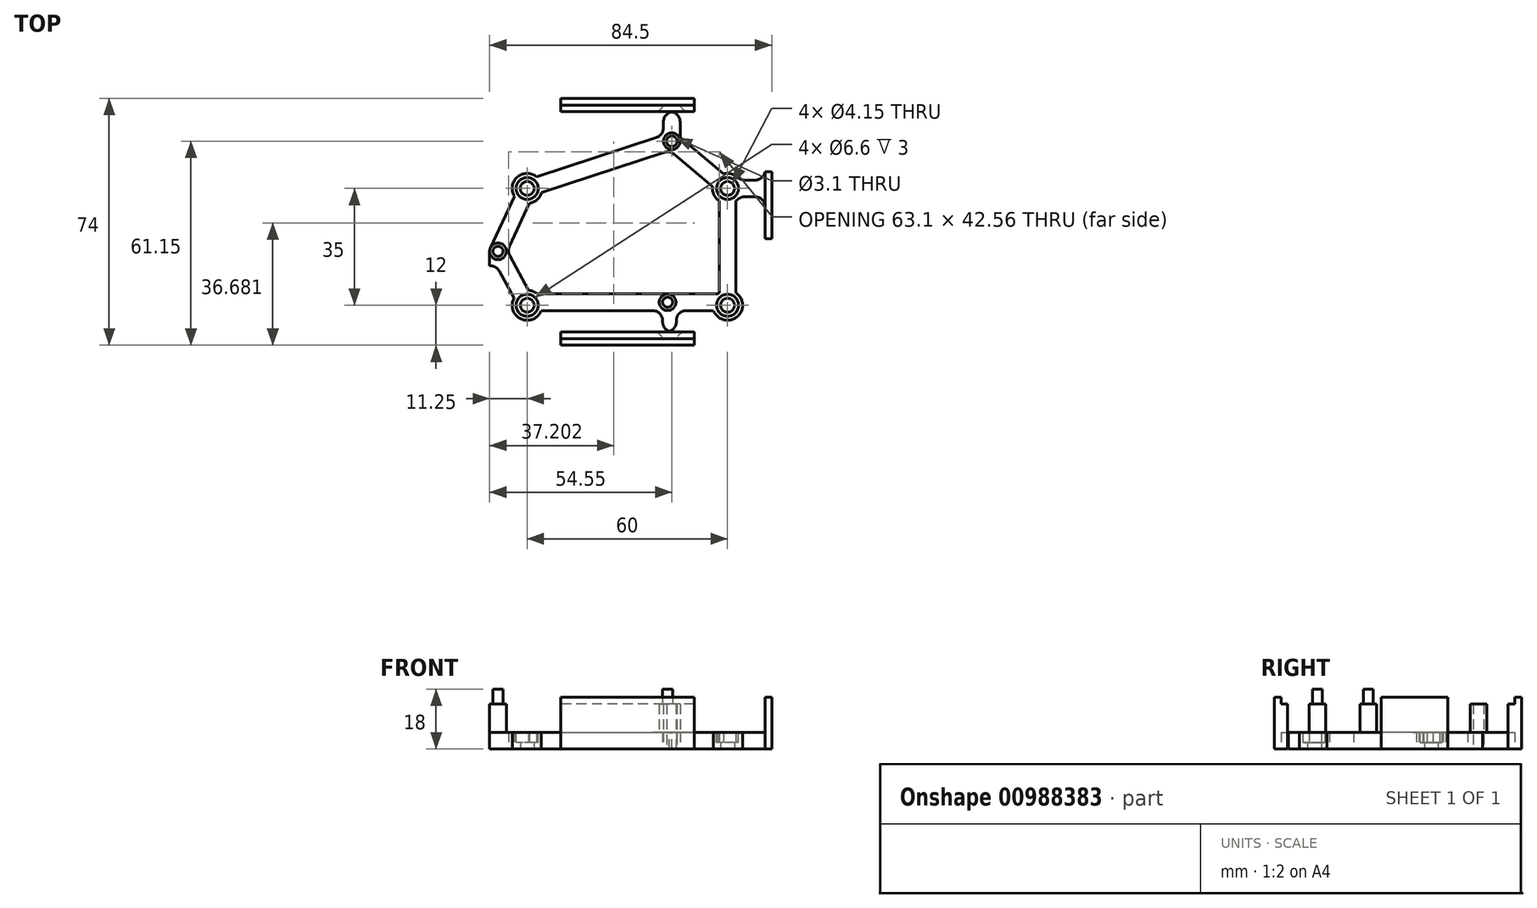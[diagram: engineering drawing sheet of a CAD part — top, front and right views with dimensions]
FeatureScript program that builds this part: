
annotation { "Feature Type Name" : "Feature", "Feature Type Description" : "" }
export const myFeature = defineFeature(function(context is Context, id is Id, definition is map)
    precondition{}
    {
        {
            var Q0;
            Q0=qCreatedBy(makeId("Top.planeOp"),FACE);
            var sketch = newSketch(context, id + "F0", { "sketchPlane" : qUnion([Q0])});
            skLineSegment(sketch, "E0.bottom", {"start": v(-41.25, 35) * mm, "end": v(41.25, 35) * mm});
            skLineSegment(sketch, "E0.top", {"start": v(-41.25, -35) * mm, "end": v(41.25, -35) * mm});
            skLineSegment(sketch, "E0.left", {"start": v(-41.25, 35) * mm, "end": v(-41.25, -35) * mm});
            skLineSegment(sketch, "E0.right", {"start": v(41.25, 35) * mm, "end": v(41.25, -35) * mm});
            skPoint(sketch, "E1", {"position": v(0, 35) * mm});
            skPoint(sketch, "E2", {"position": v(-41.25, 0) * mm});
            skCircle(sketch, "E3", {"center": v(13.3, 24.15) * mm, "radius": 1.55 * mm});
            skCircle(sketch, "E4", {"center": v(12.05, -24.1) * mm, "radius": 1.5 * mm});
            skCircle(sketch, "E5", {"center": v(-38.75, -8.85) * mm, "radius": 1.5 * mm});
            skCircle(sketch, "E6", {"center": v(-30, 10) * mm, "radius": 2.08 * mm});
            skCircle(sketch, "E7", {"center": v(30, 10) * mm, "radius": 2.08 * mm});
            skCircle(sketch, "E8", {"center": v(-30, -25) * mm, "radius": 2.08 * mm});
            skCircle(sketch, "E9", {"center": v(30, -25) * mm, "radius": 2.08 * mm});
            skLineSegment(sketch, "E10.bottom", {"start": v(-30, 10) * mm, "end": v(30, 10) * mm, "construction": true});
            skLineSegment(sketch, "E10.top", {"start": v(-30, -25) * mm, "end": v(30, -25) * mm, "construction": true});
            skLineSegment(sketch, "E10.left", {"start": v(-30, 10) * mm, "end": v(-30, -25) * mm, "construction": true});
            skLineSegment(sketch, "E10.right", {"start": v(30, 10) * mm, "end": v(30, -25) * mm, "construction": true});
            skPoint(sketch, "E11", {"position": v(0, 10) * mm});
            skPoint(sketch, "E12", {"position": v(30, -7.5) * mm});
            skLineSegment(sketch, "E13", {"start": v(-38.75, -8.85) * mm, "end": v(0, 0) * mm, "construction": true});
            skLineSegment(sketch, "E14", {"start": v(0, 0) * mm, "end": v(12.05, -24.1) * mm, "construction": true});
            skLineSegment(sketch, "E15", {"start": v(0, 0) * mm, "end": v(13.3, 24.15) * mm, "construction": true});
            skLineSegment(sketch, "E16", {"start": v(-30, 10) * mm, "end": v(13.3, 24.15) * mm, "construction": true});
            skLineSegment(sketch, "E17", {"start": v(13.3, 24.15) * mm, "end": v(30, 10) * mm, "construction": true});
            skLineSegment(sketch, "E18", {"start": v(-30, -25) * mm, "end": v(-38.75, -8.85) * mm, "construction": true});
            skLineSegment(sketch, "E19", {"start": v(-38.75, -8.85) * mm, "end": v(-30, 10) * mm, "construction": true});
            skCircle(sketch, "E20", {"center": v(-30, 10) * mm, "radius": 4.5 * mm});
            skCircle(sketch, "E21", {"center": v(30, 10) * mm, "radius": 4.5 * mm});
            skCircle(sketch, "E22", {"center": v(30, -25) * mm, "radius": 4.5 * mm});
            skCircle(sketch, "E23", {"center": v(-30, -25) * mm, "radius": 4.5 * mm});
            skCircle(sketch, "E24", {"center": v(-38.75, -8.85) * mm, "radius": 2.5 * mm});
            skCircle(sketch, "E25", {"center": v(13.3, 24.15) * mm, "radius": 2.5 * mm});
            skCircle(sketch, "E26", {"center": v(12.05, -24.1) * mm, "radius": 2.5 * mm});
            skLineSegment(sketch, "E27", {"start": v(-27.22, 13.54) * mm, "end": v(12.52, 26.53) * mm});
            skLineSegment(sketch, "E28", {"start": v(-25.67, 8.79) * mm, "end": v(14.08, 21.77) * mm});
            skLineSegment(sketch, "E29", {"start": v(28.76, 14.33) * mm, "end": v(14.92, 26.06) * mm});
            skLineSegment(sketch, "E30", {"start": v(25.53, 10.51) * mm, "end": v(11.68, 22.24) * mm});
            skLineSegment(sketch, "E31", {"start": v(27.5, 6.26) * mm, "end": v(27.5, -21.26) * mm});
            skLineSegment(sketch, "E32", {"start": v(32.5, 6.26) * mm, "end": v(32.5, -21.26) * mm});
            skLineSegment(sketch, "E33", {"start": v(27.05, -21.6) * mm, "end": v(12.05, -21.6) * mm});
            skLineSegment(sketch, "E34", {"start": v(12.05, -24.1) * mm, "end": v(30, -25) * mm, "construction": true});
            skLineSegment(sketch, "E35", {"start": v(12.05, -24.1) * mm, "end": v(-30, -25) * mm, "construction": true});
            skLineSegment(sketch, "E36", {"start": v(-27.05, -21.6) * mm, "end": v(12.05, -21.6) * mm});
            skLineSegment(sketch, "E37", {"start": v(-25.8, -26.6) * mm, "end": v(12.05, -26.6) * mm});
            skLineSegment(sketch, "E38", {"start": v(-29.58, -20.52) * mm, "end": v(-36.55, -7.66) * mm});
            skLineSegment(sketch, "E39", {"start": v(-33.98, -22.9) * mm, "end": v(-40.95, -10.04) * mm});
            skLineSegment(sketch, "E40", {"start": v(-33.84, 7.66) * mm, "end": v(-41.02, -7.8) * mm});
            skLineSegment(sketch, "E41", {"start": v(-29.3, 5.55) * mm, "end": v(-36.48, -9.9) * mm});
            skPoint(sketch, "E42", {"position": v(12.75, 21.34) * mm});
            skLineSegment(sketch, "E43", {"start": v(12.05, -26.6) * mm, "end": v(25.8, -26.6) * mm});
            skPoint(sketch, "E44", {"position": v(11.99, -26.6) * mm});
            skLineSegment(sketch, "E45.bottom", {"start": v(-20, -35) * mm, "end": v(20, -35) * mm});
            skLineSegment(sketch, "E45.top", {"start": v(-20, -37) * mm, "end": v(20, -37) * mm});
            skLineSegment(sketch, "E45.left", {"start": v(-20, -35) * mm, "end": v(-20, -37) * mm});
            skLineSegment(sketch, "E45.right", {"start": v(20, -35) * mm, "end": v(20, -37) * mm});
            skPoint(sketch, "E46", {"position": v(0, -37) * mm});
            skLineSegment(sketch, "E47.bottom", {"start": v(-20, 35) * mm, "end": v(20, 35) * mm});
            skLineSegment(sketch, "E47.top", {"start": v(-20, 37) * mm, "end": v(20, 37) * mm});
            skLineSegment(sketch, "E47.left", {"start": v(-20, 35) * mm, "end": v(-20, 37) * mm});
            skLineSegment(sketch, "E47.right", {"start": v(20, 35) * mm, "end": v(20, 37) * mm});
            skPoint(sketch, "E48", {"position": v(0, 37) * mm});
            skLineSegment(sketch, "E49.bottom", {"start": v(41.25, 15) * mm, "end": v(43.25, 15) * mm});
            skLineSegment(sketch, "E49.top", {"start": v(41.25, -5) * mm, "end": v(43.25, -5) * mm});
            skLineSegment(sketch, "E49.left", {"start": v(41.25, 15) * mm, "end": v(41.25, -5) * mm});
            skLineSegment(sketch, "E49.right", {"start": v(43.25, 15) * mm, "end": v(43.25, -5) * mm});
            skLineSegment(sketch, "E50.bottom", {"start": v(-41.25, -35) * mm, "end": v(-39.25, -35) * mm});
            skLineSegment(sketch, "E50.top", {"start": v(-41.25, -13.18) * mm, "end": v(-39.25, -13.18) * mm});
            skLineSegment(sketch, "E50.left", {"start": v(-41.25, -35) * mm, "end": v(-41.25, -13.18) * mm});
            skLineSegment(sketch, "E50.right", {"start": v(-39.25, -35) * mm, "end": v(-39.25, -13.18) * mm});
            skLineSegment(sketch, "E51", {"start": v(10.55, -26.1) * mm, "end": v(10.55, -35) * mm});
            skLineSegment(sketch, "E52", {"start": v(14.55, -24.05) * mm, "end": v(14.78, -35) * mm});
            skLineSegment(sketch, "E53", {"start": v(33.74, 12.5) * mm, "end": v(41.25, 12.5) * mm});
            skLineSegment(sketch, "E54", {"start": v(33.74, 7.5) * mm, "end": v(41.25, 7.5) * mm});
            skLineSegment(sketch, "E55", {"start": v(41.25, 12.5) * mm, "end": v(41.25, 7.5) * mm, "construction": true});
            skPoint(sketch, "E56", {"position": v(41.25, 10) * mm});
            skLineSegment(sketch, "E57", {"start": v(10.8, 24.15) * mm, "end": v(10.8, 35) * mm});
            skLineSegment(sketch, "E58", {"start": v(15.8, 24.15) * mm, "end": v(15.8, 35) * mm});
            skLineSegment(sketch, "E59.top", {"start": v(-20, -33) * mm, "end": v(20, -33) * mm});
            skLineSegment(sketch, "E59.left", {"start": v(-20, -35) * mm, "end": v(-20, -33) * mm});
            skLineSegment(sketch, "E59.right", {"start": v(20, -35) * mm, "end": v(20, -33) * mm});
            skLineSegment(sketch, "E60.top", {"start": v(-20, 33) * mm, "end": v(20, 33) * mm});
            skLineSegment(sketch, "E60.left", {"start": v(-20, 35) * mm, "end": v(-20, 33) * mm});
            skLineSegment(sketch, "E60.right", {"start": v(20, 35) * mm, "end": v(20, 33) * mm});
            skSolve(sketch);
        }
        {
            var Q0;
            {var subQ1=sQuery(id+"F0.wireOp",EDGE,"E20");var subQ9=sQuery(id+"F0.wireOp",EDGE,"E27");var subQ10=makeQuery(id+"F0.imprint","INTERSECT",VERTEX,{"derivedFrom":[subQ1,subQ9]});Q0=makeQuery(id+"F0.imprint","IMPRINT",FACE,{"disambiguationData":[TD([[makeQuery(id+"F0.imprint","IMPRINT",EDGE,{"disambiguationData":[TD([[subQ10,1.0]])],"derivedFrom":subQ1}),-1.0]])]});}
            var Q1;
            Q1=makeQuery(id+"F0.imprint","IMPRINT",FACE,{"disambiguationData":[TD([[makeQuery(id+"F0.imprint","IMPRINT",EDGE,{"derivedFrom":sQuery(id+"F0.wireOp",EDGE,"E6")}),-1.0]])]});
            var Q2;
            {var subQ0=sQuery(id+"F0.wireOp",EDGE,"E40");Q2=makeQuery(id+"F0.imprint","IMPRINT",FACE,{"disambiguationData":[TD([[makeQuery(id+"F0.imprint","IMPRINT",EDGE,{"derivedFrom":subQ0}),1.0]])]});}
            var Q3;
            Q3=makeQuery(id+"F0.imprint","IMPRINT",FACE,{"disambiguationData":[TD([[makeQuery(id+"F0.imprint","IMPRINT",EDGE,{"derivedFrom":sQuery(id+"F0.wireOp",EDGE,"E5")}),-1.0]])]});
            var Q4;
            {var subQ0=sQuery(id+"F0.wireOp",EDGE,"E50.top");Q4=makeQuery(id+"F0.imprint","IMPRINT",FACE,{"disambiguationData":[TD([[makeQuery(id+"F0.imprint","IMPRINT",EDGE,{"derivedFrom":subQ0}),1.0]])]});}
            var Q5;
            {var subQ0=sQuery(id+"F0.wireOp",EDGE,"E38");var subQ1=sQuery(id+"F0.wireOp",EDGE,"E24");var subQ2=makeQuery(id+"F0.imprint","INTERSECT",VERTEX,{"derivedFrom":[subQ1,subQ0]});Q5=makeQuery(id+"F0.imprint","IMPRINT",FACE,{"disambiguationData":[TD([[makeQuery(id+"F0.imprint","IMPRINT",EDGE,{"disambiguationData":[TD([[subQ2,1.0]])],"derivedFrom":subQ1}),-1.0]])]});}
            var Q6;
            {var subQ1=sQuery(id+"F0.wireOp",EDGE,"E23");var subQ8=sQuery(id+"F0.wireOp",EDGE,"E38");var subQ9=makeQuery(id+"F0.imprint","INTERSECT",VERTEX,{"derivedFrom":[subQ1,subQ8]});Q6=makeQuery(id+"F0.imprint","IMPRINT",FACE,{"disambiguationData":[TD([[makeQuery(id+"F0.imprint","IMPRINT",EDGE,{"disambiguationData":[TD([[subQ9,-1.0]])],"derivedFrom":subQ1}),-1.0]])]});}
            var Q7;
            Q7=makeQuery(id+"F0.imprint","IMPRINT",FACE,{"disambiguationData":[TD([[makeQuery(id+"F0.imprint","IMPRINT",EDGE,{"derivedFrom":sQuery(id+"F0.wireOp",EDGE,"E50.bottom")}),1.0]])]});
            var Q8;
            Q8=makeQuery(id+"F0.imprint","IMPRINT",FACE,{"disambiguationData":[TD([[makeQuery(id+"F0.imprint","IMPRINT",EDGE,{"derivedFrom":sQuery(id+"F0.wireOp",EDGE,"E8")}),-1.0]])]});
            var Q9;
            {var subQ0=sQuery(id+"F0.wireOp",EDGE,"E36");Q9=makeQuery(id+"F0.imprint","IMPRINT",FACE,{"disambiguationData":[TD([[makeQuery(id+"F0.imprint","IMPRINT",EDGE,{"derivedFrom":subQ0}),-1.0]])]});}
            var Q10;
            {var subQ0=sQuery(id+"F0.wireOp",EDGE,"E43");var subQ1=sQuery(id+"F0.wireOp",EDGE,"E26");var subQ2=makeQuery(id+"F0.imprint","INTERSECT",VERTEX,{"derivedFrom":[subQ1,subQ0]});Q10=makeQuery(id+"F0.imprint","IMPRINT",FACE,{"disambiguationData":[TD([[makeQuery(id+"F0.imprint","IMPRINT",EDGE,{"disambiguationData":[TD([[subQ2,1.0]])],"derivedFrom":subQ1}),-1.0]])]});}
            var Q11;
            Q11=makeQuery(id+"F0.imprint","IMPRINT",FACE,{"disambiguationData":[TD([[makeQuery(id+"F0.imprint","IMPRINT",EDGE,{"derivedFrom":sQuery(id+"F0.wireOp",EDGE,"E4")}),-1.0]])]});
            var Q12;
            Q12=makeQuery(id+"F0.imprint","IMPRINT",FACE,{"disambiguationData":[TD([[makeQuery(id+"F0.imprint","IMPRINT",EDGE,{"derivedFrom":sQuery(id+"F0.wireOp",EDGE,"E4")}),1.0]])]});
            var Q13;
            {var subQ0=sQuery(id+"F0.wireOp",EDGE,"E37");var subQ1=sQuery(id+"F0.wireOp",EDGE,"E26");var subQ2=makeQuery(id+"F0.imprint","INTERSECT",VERTEX,{"derivedFrom":[subQ1,subQ0]});Q13=makeQuery(id+"F0.imprint","IMPRINT",FACE,{"disambiguationData":[TD([[makeQuery(id+"F0.imprint","IMPRINT",EDGE,{"disambiguationData":[TD([[subQ2,1.0]])],"derivedFrom":subQ1}),-1.0]])]});}
            var Q14;
            {var subQ0=sQuery(id+"F0.wireOp",EDGE,"E51");var subQ5=sQuery(id+"F0.wireOp",EDGE,"E37");var subQ6=makeQuery(id+"F0.imprint","INTERSECT",VERTEX,{"derivedFrom":[subQ5,subQ0]});Q14=makeQuery(id+"F0.imprint","IMPRINT",FACE,{"disambiguationData":[TD([[makeQuery(id+"F0.imprint","IMPRINT",EDGE,{"disambiguationData":[TD([[subQ6,-1.0]])],"derivedFrom":subQ5}),-1.0]])]});}
            var Q15;
            {var subQ0=sQuery(id+"F0.wireOp",EDGE,"E37");var subQ1=sQuery(id+"F0.wireOp",EDGE,"E26");var subQ2=makeQuery(id+"F0.imprint","INTERSECT",VERTEX,{"derivedFrom":[subQ1,subQ0]});Q15=makeQuery(id+"F0.imprint","IMPRINT",FACE,{"disambiguationData":[TD([[makeQuery(id+"F0.imprint","IMPRINT",EDGE,{"disambiguationData":[TD([[subQ2,-1.0]])],"derivedFrom":subQ1}),-1.0]])]});}
            var Q16;
            {var subQ0=sQuery(id+"F0.wireOp",EDGE,"E33");Q16=makeQuery(id+"F0.imprint","IMPRINT",FACE,{"disambiguationData":[TD([[makeQuery(id+"F0.imprint","IMPRINT",EDGE,{"derivedFrom":subQ0}),1.0]])]});}
            var Q17;
            Q17=makeQuery(id+"F0.imprint","IMPRINT",FACE,{"disambiguationData":[TD([[makeQuery(id+"F0.imprint","IMPRINT",EDGE,{"derivedFrom":sQuery(id+"F0.wireOp",EDGE,"E45.top")}),1.0]])]});
            var Q18;
            Q18=makeQuery(id+"F0.imprint","IMPRINT",FACE,{"disambiguationData":[TD([[makeQuery(id+"F0.imprint","IMPRINT",EDGE,{"derivedFrom":sQuery(id+"F0.wireOp",EDGE,"E9")}),-1.0]])]});
            var Q19;
            {var subQ0=sQuery(id+"F0.wireOp",EDGE,"E31");Q19=makeQuery(id+"F0.imprint","IMPRINT",FACE,{"disambiguationData":[TD([[makeQuery(id+"F0.imprint","IMPRINT",EDGE,{"derivedFrom":subQ0}),1.0]])]});}
            var Q20;
            Q20=makeQuery(id+"F0.imprint","IMPRINT",FACE,{"disambiguationData":[TD([[makeQuery(id+"F0.imprint","IMPRINT",EDGE,{"derivedFrom":sQuery(id+"F0.wireOp",EDGE,"E7")}),-1.0]])]});
            var Q21;
            {var subQ0=sQuery(id+"F0.wireOp",EDGE,"E53");Q21=makeQuery(id+"F0.imprint","IMPRINT",FACE,{"disambiguationData":[TD([[makeQuery(id+"F0.imprint","IMPRINT",EDGE,{"derivedFrom":subQ0}),-1.0]])]});}
            var Q22;
            {var subQ3=sQuery(id+"F0.wireOp",EDGE,"E49.bottom");Q22=makeQuery(id+"F0.imprint","IMPRINT",FACE,{"disambiguationData":[TD([[makeQuery(id+"F0.imprint","IMPRINT",EDGE,{"derivedFrom":subQ3}),-1.0]])]});}
            var Q23;
            {var subQ0=sQuery(id+"F0.wireOp",EDGE,"E28");var subQ1=sQuery(id+"F0.wireOp",EDGE,"E25");var subQ2=makeQuery(id+"F0.imprint","INTERSECT",VERTEX,{"derivedFrom":[subQ1,subQ0]});Q23=makeQuery(id+"F0.imprint","IMPRINT",FACE,{"disambiguationData":[TD([[makeQuery(id+"F0.imprint","IMPRINT",EDGE,{"disambiguationData":[TD([[subQ2,1.0]])],"derivedFrom":subQ1}),-1.0]])]});}
            var Q24;
            Q24=makeQuery(id+"F0.imprint","IMPRINT",FACE,{"disambiguationData":[TD([[makeQuery(id+"F0.imprint","IMPRINT",EDGE,{"derivedFrom":sQuery(id+"F0.wireOp",EDGE,"E3")}),-1.0]])]});
            var Q25;
            Q25=makeQuery(id+"F0.imprint","IMPRINT",FACE,{"disambiguationData":[TD([[makeQuery(id+"F0.imprint","IMPRINT",EDGE,{"derivedFrom":sQuery(id+"F0.wireOp",EDGE,"E3")}),1.0]])]});
            var Q26;
            {var subQ0=sQuery(id+"F0.wireOp",EDGE,"E29");var subQ1=sQuery(id+"F0.wireOp",EDGE,"E21");var subQ2=makeQuery(id+"F0.imprint","INTERSECT",VERTEX,{"derivedFrom":[subQ1,subQ0]});Q26=makeQuery(id+"F0.imprint","IMPRINT",FACE,{"disambiguationData":[TD([[makeQuery(id+"F0.imprint","IMPRINT",EDGE,{"disambiguationData":[TD([[subQ2,-1.0]])],"derivedFrom":subQ1}),-1.0]])]});}
            var Q27;
            {var subQ0=sQuery(id+"F0.wireOp",EDGE,"E27");var subQ1=sQuery(id+"F0.wireOp",EDGE,"E25");var subQ2=makeQuery(id+"F0.imprint","INTERSECT",VERTEX,{"derivedFrom":[subQ1,subQ0]});Q27=makeQuery(id+"F0.imprint","IMPRINT",FACE,{"disambiguationData":[TD([[makeQuery(id+"F0.imprint","IMPRINT",EDGE,{"disambiguationData":[TD([[subQ2,-1.0]])],"derivedFrom":subQ1}),-1.0]])]});}
            var Q28;
            {var subQ0=sQuery(id+"F0.wireOp",EDGE,"E29");var subQ1=sQuery(id+"F0.wireOp",EDGE,"E25");var subQ2=makeQuery(id+"F0.imprint","INTERSECT",VERTEX,{"derivedFrom":[subQ1,subQ0]});Q28=makeQuery(id+"F0.imprint","IMPRINT",FACE,{"disambiguationData":[TD([[makeQuery(id+"F0.imprint","IMPRINT",EDGE,{"disambiguationData":[TD([[subQ2,1.0]])],"derivedFrom":subQ1}),-1.0]])]});}
            var Q29;
            {var subQ5=sQuery(id+"F0.wireOp",EDGE,"E27");var subQ8=sQuery(id+"F0.wireOp",EDGE,"E25");var subQ11=makeQuery(id+"F0.imprint","INTERSECT",VERTEX,{"derivedFrom":[subQ8,subQ5]});Q29=makeQuery(id+"F0.imprint","IMPRINT",FACE,{"disambiguationData":[TD([[makeQuery(id+"F0.imprint","IMPRINT",EDGE,{"disambiguationData":[TD([[subQ11,1.0]])],"derivedFrom":subQ8}),-1.0]])]});}
            var Q30;
            Q30=makeQuery(id+"F0.imprint","IMPRINT",FACE,{"disambiguationData":[TD([[makeQuery(id+"F0.imprint","IMPRINT",EDGE,{"derivedFrom":sQuery(id+"F0.wireOp",EDGE,"E47.top")}),-1.0]])]});
            var Q31;
            Q31=makeQuery(id+"F0.imprint","IMPRINT",FACE,{"disambiguationData":[TD([[makeQuery(id+"F0.imprint","IMPRINT",EDGE,{"derivedFrom":sQuery(id+"F0.wireOp",EDGE,"E5")}),1.0]])]});
            var Q32;
            {var subQ5=sQuery(id+"F0.wireOp",EDGE,"E60.left");Q32=makeQuery(id+"F0.imprint","IMPRINT",FACE,{"disambiguationData":[TD([[makeQuery(id+"F0.imprint","IMPRINT",EDGE,{"derivedFrom":subQ5}),1.0]])]});}
            var Q33;
            {var subQ5=sQuery(id+"F0.wireOp",EDGE,"E60.right");Q33=makeQuery(id+"F0.imprint","IMPRINT",FACE,{"disambiguationData":[TD([[makeQuery(id+"F0.imprint","IMPRINT",EDGE,{"derivedFrom":subQ5}),-1.0]])]});}
            var Q34;
            {var subQ0=sQuery(id+"F0.wireOp",EDGE,"E47.bottom");var subQ1=sQuery(id+"F0.wireOp",EDGE,"E57");var subQ2=makeQuery(id+"F0.imprint","INTERSECT",VERTEX,{"derivedFrom":[subQ1,subQ0]});Q34=makeQuery(id+"F0.imprint","IMPRINT",FACE,{"disambiguationData":[TD([[makeQuery(id+"F0.imprint","IMPRINT",EDGE,{"disambiguationData":[TD([[subQ2,1.0]])],"derivedFrom":subQ1}),-1.0]])]});}
            var Q35;
            {var subQ0=sQuery(id+"F0.wireOp",EDGE,"E45.bottom");var subQ1=sQuery(id+"F0.wireOp",EDGE,"E51");var subQ2=makeQuery(id+"F0.imprint","INTERSECT",VERTEX,{"derivedFrom":[subQ1,subQ0]});Q35=makeQuery(id+"F0.imprint","IMPRINT",FACE,{"disambiguationData":[TD([[makeQuery(id+"F0.imprint","IMPRINT",EDGE,{"disambiguationData":[TD([[subQ2,1.0]])],"derivedFrom":subQ1}),1.0]])]});}
            var Q36;
            {var subQ5=sQuery(id+"F0.wireOp",EDGE,"E59.right");Q36=makeQuery(id+"F0.imprint","IMPRINT",FACE,{"disambiguationData":[TD([[makeQuery(id+"F0.imprint","IMPRINT",EDGE,{"derivedFrom":subQ5}),1.0]])]});}
            var Q37;
            {var subQ5=sQuery(id+"F0.wireOp",EDGE,"E59.left");Q37=makeQuery(id+"F0.imprint","IMPRINT",FACE,{"disambiguationData":[TD([[makeQuery(id+"F0.imprint","IMPRINT",EDGE,{"derivedFrom":subQ5}),-1.0]])]});}
            var Q38;
            {var subQ0=sQuery(id+"F0.wireOp",EDGE,"E32");Q38=makeQuery(id+"F0.imprint","IMPRINT",FACE,{"disambiguationData":[TD([[makeQuery(id+"F0.imprint","IMPRINT",EDGE,{"derivedFrom":subQ0}),-1.0]])]});}
            extrude(context, id + "F1", {"entities" : qUnion([Q0, Q1, Q2, Q3, Q4, Q5, Q6, Q7, Q8, Q9, Q10, Q11, Q12, Q13, Q14, Q15, Q16, Q17, Q18, Q19, Q20, Q21, Q22, Q23, Q24, Q25, Q26, Q27, Q28, Q29, Q30, Q31, Q32, Q33, Q34, Q35, Q36, Q37, Q38]), "depth" : 5 * mm, "offsetDistance" : 25 * mm});
        }
        {
            var Q0;
            Q0=makeQuery(id+"F1.opExtrude","CAP_FACE",FACE,{"disambiguationData":[OSD([sQuery(id+"F0.wireOp",EDGE,"E0.left"),sQuery(id+"F0.wireOp",EDGE,"E5"),sQuery(id+"F0.wireOp",EDGE,"E6"),sQuery(id+"F0.wireOp",EDGE,"E7"),sQuery(id+"F0.wireOp",EDGE,"E8"),sQuery(id+"F0.wireOp",EDGE,"E9"),sQuery(id+"F0.wireOp",EDGE,"E20"),sQuery(id+"F0.wireOp",EDGE,"E21"),sQuery(id+"F0.wireOp",EDGE,"E22"),sQuery(id+"F0.wireOp",EDGE,"E23"),sQuery(id+"F0.wireOp",EDGE,"E24"),sQuery(id+"F0.wireOp",EDGE,"E26"),sQuery(id+"F0.wireOp",EDGE,"E27"),sQuery(id+"F0.wireOp",EDGE,"E28"),sQuery(id+"F0.wireOp",EDGE,"E29"),sQuery(id+"F0.wireOp",EDGE,"E30"),sQuery(id+"F0.wireOp",EDGE,"E31"),sQuery(id+"F0.wireOp",EDGE,"E32"),sQuery(id+"F0.wireOp",EDGE,"E33"),sQuery(id+"F0.wireOp",EDGE,"E36"),sQuery(id+"F0.wireOp",EDGE,"E37"),sQuery(id+"F0.wireOp",EDGE,"E38"),sQuery(id+"F0.wireOp",EDGE,"E39"),sQuery(id+"F0.wireOp",EDGE,"E40"),sQuery(id+"F0.wireOp",EDGE,"E41"),sQuery(id+"F0.wireOp",EDGE,"E43"),sQuery(id+"F0.wireOp",EDGE,"E45.bottom"),sQuery(id+"F0.wireOp",EDGE,"E45.top"),sQuery(id+"F0.wireOp",EDGE,"E45.left"),sQuery(id+"F0.wireOp",EDGE,"E45.right"),sQuery(id+"F0.wireOp",EDGE,"E47.bottom"),sQuery(id+"F0.wireOp",EDGE,"E47.top"),sQuery(id+"F0.wireOp",EDGE,"E47.left"),sQuery(id+"F0.wireOp",EDGE,"E47.right"),sQuery(id+"F0.wireOp",EDGE,"E49.bottom"),sQuery(id+"F0.wireOp",EDGE,"E49.top"),sQuery(id+"F0.wireOp",EDGE,"E49.left"),sQuery(id+"F0.wireOp",EDGE,"E49.right"),sQuery(id+"F0.wireOp",EDGE,"E50.bottom"),sQuery(id+"F0.wireOp",EDGE,"E50.left"),sQuery(id+"F0.wireOp",EDGE,"E50.right"),sQuery(id+"F0.wireOp",EDGE,"E51"),sQuery(id+"F0.wireOp",EDGE,"E52"),sQuery(id+"F0.wireOp",EDGE,"E53"),sQuery(id+"F0.wireOp",EDGE,"E54"),sQuery(id+"F0.wireOp",EDGE,"E57"),sQuery(id+"F0.wireOp",EDGE,"E58")])],"isStart":false});
            var sketch = newSketch(context, id + "F2", { "sketchPlane" : qUnion([Q0])});
            skCircle(sketch, "E61.0", {"center": v(13.3, 24.15) * mm, "radius": 2.5 * mm});
            skCircle(sketch, "E62.0", {"center": v(-38.75, -8.85) * mm, "radius": 2.5 * mm});
            skCircle(sketch, "E63.0", {"center": v(12.05, -24.1) * mm, "radius": 2.5 * mm});
            skLineSegment(sketch, "E64.0", {"start": v(43.25, 15) * mm, "end": v(43.25, -5) * mm});
            skLineSegment(sketch, "E65.0", {"start": v(41.25, 15) * mm, "end": v(43.25, 15) * mm});
            skLineSegment(sketch, "E65.1", {"start": v(41.25, -5) * mm, "end": v(43.25, -5) * mm});
            skLineSegment(sketch, "E65.2", {"start": v(-20, 37) * mm, "end": v(20, 37) * mm});
            skLineSegment(sketch, "E65.3", {"start": v(-20, 35) * mm, "end": v(-20, 37) * mm});
            skLineSegment(sketch, "E66", {"start": v(41.25, 15) * mm, "end": v(41.25, -5) * mm});
            skLineSegment(sketch, "E67", {"start": v(-20, -37) * mm, "end": v(20, -37) * mm});
            skLineSegment(sketch, "E68", {"start": v(-41.25, -35) * mm, "end": v(-39.25, -35) * mm});
            skLineSegment(sketch, "E69", {"start": v(-39.25, -35) * mm, "end": v(-39.25, -13.18) * mm});
            skLineSegment(sketch, "E70", {"start": v(-39.25, -13.18) * mm, "end": v(-41.25, -13.18) * mm});
            skLineSegment(sketch, "E71", {"start": v(-41.25, -13.18) * mm, "end": v(-41.25, -8.85) * mm});
            skLineSegment(sketch, "E72", {"start": v(-39.25, -13.18) * mm, "end": v(-39.25, -11.3) * mm});
            skLineSegment(sketch, "E73", {"start": v(-20, 35) * mm, "end": v(-20, 33) * mm});
            skLineSegment(sketch, "E74", {"start": v(-20, 33) * mm, "end": v(20, 33) * mm});
            skLineSegment(sketch, "E75", {"start": v(20, 33) * mm, "end": v(20, 37) * mm});
            skLineSegment(sketch, "E76", {"start": v(-20, -37) * mm, "end": v(-20, -33) * mm});
            skLineSegment(sketch, "E77", {"start": v(-20, -33) * mm, "end": v(20, -33) * mm});
            skLineSegment(sketch, "E78", {"start": v(20, -33) * mm, "end": v(20, -37) * mm});
            skSolve(sketch);
        }
        {
            var Q0;
            {var subQ0=sQuery(id+"F2.wireOp",EDGE,"E68");Q0=makeQuery(id+"F2.imprint","IMPRINT",FACE,{"disambiguationData":[TD([[makeQuery(id+"F2.imprint","IMPRINT",EDGE,{"derivedFrom":subQ0}),1.0]])]});}
            var Q1;
            {var subQ0=sQuery(id+"F2.wireOp",EDGE,"E62.0");var subQ1=makeQuery(id+"F2.imprint","INTERSECT",VERTEX,{"derivedFrom":[makeQuery(id+"F1.opExtrude","CAP_EDGE",EDGE,{"disambiguationData":[OSD([sQuery(id+"F0.wireOp",EDGE,"E40")])],"isStart":false}),subQ0]});Q1=makeQuery(id+"F2.imprint","IMPRINT",FACE,{"disambiguationData":[TD([[makeQuery(id+"F2.imprint","IMPRINT",EDGE,{"disambiguationData":[TD([[subQ1,-1.0]])],"derivedFrom":subQ0}),1.0]])]});}
            var Q2;
            Q2=makeQuery(id+"F2.imprint","IMPRINT",FACE,{"disambiguationData":[TD([[makeQuery(id+"F2.imprint","IMPRINT",EDGE,{"derivedFrom":sQuery(id+"F2.wireOp",EDGE,"E61.0")}),1.0]])]});
            var Q3;
            Q3=makeQuery(id+"F2.imprint","IMPRINT",FACE,{"disambiguationData":[TD([[makeQuery(id+"F2.imprint","IMPRINT",EDGE,{"derivedFrom":sQuery(id+"F2.wireOp",EDGE,"E65.2")}),-1.0]])]});
            var Q4;
            Q4=makeQuery(id+"F2.imprint","IMPRINT",FACE,{"disambiguationData":[TD([[makeQuery(id+"F2.imprint","IMPRINT",EDGE,{"derivedFrom":sQuery(id+"F2.wireOp",EDGE,"E64.0")}),-1.0]])]});
            var Q5;
            Q5=makeQuery(id+"F2.imprint","IMPRINT",FACE,{"disambiguationData":[TD([[makeQuery(id+"F2.imprint","IMPRINT",EDGE,{"derivedFrom":makeQuery(id+"F1.opExtrude","CAP_EDGE",EDGE,{"disambiguationData":[OSD([sQuery(id+"F0.wireOp",EDGE,"E45.top")])],"isStart":false})}),1.0]])]});
            var Q6;
            Q6=makeQuery(id+"F2.imprint","IMPRINT",FACE,{"disambiguationData":[TD([[makeQuery(id+"F2.imprint","IMPRINT",EDGE,{"derivedFrom":sQuery(id+"F2.wireOp",EDGE,"E70")}),-1.0]])]});
            var Q7;
            {var subQ0=sQuery(id+"F2.wireOp",EDGE,"E63.0");var subQ1=makeQuery(id+"F2.imprint","INTERSECT",VERTEX,{"derivedFrom":[makeQuery(id+"F1.opExtrude","CAP_EDGE",EDGE,{"disambiguationData":[OSD([sQuery(id+"F0.wireOp",EDGE,"E33")])],"isStart":false}),subQ0]});Q7=makeQuery(id+"F2.imprint","IMPRINT",FACE,{"disambiguationData":[TD([[makeQuery(id+"F2.imprint","IMPRINT",EDGE,{"disambiguationData":[TD([[subQ1,-1.0]])],"derivedFrom":subQ0}),1.0]])]});}
            var Q8;
            Q8=makeQuery(id+"F2.imprint","IMPRINT",FACE,{"disambiguationData":[TD([[makeQuery(id+"F2.imprint","IMPRINT",EDGE,{"derivedFrom":sQuery(id+"F2.wireOp",EDGE,"E67")}),1.0]])]});
            extrude(context, id + "F3", {"entities" : qUnion([Q0, Q1, Q2, Q3, Q4, Q5, Q6, Q7, Q8]), "operationType" : NewBodyOperationType.ADD, "depth" : 8.5 * mm, "offsetDistance" : 25 * mm});
        }
        {
            var Q0;
            Q0=makeQuery(id+"F0.imprint","IMPRINT",FACE,{"disambiguationData":[TD([[makeQuery(id+"F0.imprint","IMPRINT",EDGE,{"derivedFrom":sQuery(id+"F0.wireOp",EDGE,"E50.bottom")}),1.0]])]});
            var Q1;
            Q1=makeQuery(id+"F0.imprint","IMPRINT",FACE,{"disambiguationData":[TD([[makeQuery(id+"F0.imprint","IMPRINT",EDGE,{"derivedFrom":sQuery(id+"F0.wireOp",EDGE,"E45.top")}),1.0]])]});
            var Q2;
            Q2=makeQuery(id+"F0.imprint","IMPRINT",FACE,{"disambiguationData":[TD([[makeQuery(id+"F0.imprint","IMPRINT",EDGE,{"derivedFrom":sQuery(id+"F0.wireOp",EDGE,"E47.top")}),-1.0]])]});
            var Q3;
            {var subQ3=sQuery(id+"F0.wireOp",EDGE,"E49.bottom");Q3=makeQuery(id+"F0.imprint","IMPRINT",FACE,{"disambiguationData":[TD([[makeQuery(id+"F0.imprint","IMPRINT",EDGE,{"derivedFrom":subQ3}),-1.0]])]});}
            var Q4;
            Q4=makeQuery(id+"F0.imprint","IMPRINT",FACE,{"disambiguationData":[TD([[makeQuery(id+"F0.imprint","IMPRINT",EDGE,{"derivedFrom":sQuery(id+"F0.wireOp",EDGE,"E5")}),1.0]])]});
            var Q5;
            Q5=makeQuery(id+"F0.imprint","IMPRINT",FACE,{"disambiguationData":[TD([[makeQuery(id+"F0.imprint","IMPRINT",EDGE,{"derivedFrom":sQuery(id+"F0.wireOp",EDGE,"E4")}),1.0]])]});
            extrude(context, id + "F4", {"entities" : qUnion([Q0, Q1, Q2, Q3, Q4, Q5]), "operationType" : NewBodyOperationType.ADD, "depth" : 11 * mm, "offsetDistance" : 25 * mm});
        }
        {
            var Q0;
            Q0=makeQuery(id+"F0.imprint","IMPRINT",FACE,{"disambiguationData":[TD([[makeQuery(id+"F0.imprint","IMPRINT",EDGE,{"derivedFrom":sQuery(id+"F0.wireOp",EDGE,"E3")}),1.0]])]});
            var Q1;
            Q1=makeQuery(id+"F3.opExtrude","CAP_FACE",FACE,{"disambiguationData":[OSD([sQuery(id+"F2.wireOp",EDGE,"E61.0")])],"isStart":false});
            extrude(context, id + "F5", {"entities" : qUnion([Q0]), "operationType" : NewBodyOperationType.REMOVE, "endBound" : BoundingType.UP_TO_SURFACE, "depth" : 25 * mm, "endBoundEntityFace" : qUnion([Q1]), "offsetDistance" : 25 * mm});
        }
        {
            var Q0;
            Q0=makeQuery(id+"F1.opExtrude","SWEPT_EDGE",EDGE,{"disambiguationData":[OSD([sQuery(id+"F0.wireOp",EDGE,"E39"),sQuery(id+"F0.wireOp",EDGE,"E50.top"),sQuery(id+"F0.wireOp",EDGE,"E50.right")])]});
            var Q1;
            Q1=makeQuery(id+"F1.opExtrude","SWEPT_EDGE",EDGE,{"disambiguationData":[OSD([sQuery(id+"F0.wireOp",EDGE,"E58"),sQuery(id+"F0.wireOp",EDGE,"E60.top")])]});
            var Q2;
            Q2=makeQuery(id+"F1.opExtrude","SWEPT_EDGE",EDGE,{"disambiguationData":[OSD([sQuery(id+"F0.wireOp",EDGE,"E49.left"),sQuery(id+"F0.wireOp",EDGE,"E53")])]});
            var Q3;
            Q3=makeQuery(id+"F1.opExtrude","SWEPT_EDGE",EDGE,{"disambiguationData":[OSD([sQuery(id+"F0.wireOp",EDGE,"E49.left"),sQuery(id+"F0.wireOp",EDGE,"E54")])]});
            var Q4;
            Q4=makeQuery(id+"F1.opExtrude","SWEPT_EDGE",EDGE,{"disambiguationData":[OSD([sQuery(id+"F0.wireOp",EDGE,"E52"),sQuery(id+"F0.wireOp",EDGE,"E59.top")])]});
            var Q5;
            Q5=makeQuery(id+"F1.opExtrude","SWEPT_EDGE",EDGE,{"disambiguationData":[OSD([sQuery(id+"F0.wireOp",EDGE,"E43"),sQuery(id+"F0.wireOp",EDGE,"E52")])]});
            var Q6;
            Q6=makeQuery(id+"F1.opExtrude","SWEPT_EDGE",EDGE,{"disambiguationData":[OSD([sQuery(id+"F0.wireOp",EDGE,"E28"),sQuery(id+"F0.wireOp",EDGE,"E30")])]});
            var Q7;
            Q7=makeQuery(id+"F1.opExtrude","SWEPT_EDGE",EDGE,{"disambiguationData":[OSD([sQuery(id+"F0.wireOp",EDGE,"E38"),sQuery(id+"F0.wireOp",EDGE,"E41")])]});
            var Q8;
            Q8=makeQuery(id+"F1.opExtrude","SWEPT_EDGE",EDGE,{"disambiguationData":[OSD([sQuery(id+"F0.wireOp",EDGE,"E37"),sQuery(id+"F0.wireOp",EDGE,"E51")])]});
            var Q9;
            Q9=makeQuery(id+"F1.opExtrude","SWEPT_EDGE",EDGE,{"disambiguationData":[OSD([sQuery(id+"F0.wireOp",EDGE,"E51"),sQuery(id+"F0.wireOp",EDGE,"E59.top")])]});
            var Q10;
            Q10=makeQuery(id+"F1.opExtrude","SWEPT_EDGE",EDGE,{"disambiguationData":[OSD([sQuery(id+"F0.wireOp",EDGE,"E57"),sQuery(id+"F0.wireOp",EDGE,"E60.top")])]});
            var Q11;
            Q11=makeQuery(id+"F1.opExtrude","SWEPT_EDGE",EDGE,{"disambiguationData":[OSD([sQuery(id+"F0.wireOp",EDGE,"E27"),sQuery(id+"F0.wireOp",EDGE,"E57")])]});
            fillet(context, id + "F6", {"entities" : qUnion([Q0, Q1, Q2, Q3, Q4, Q5, Q6, Q7, Q8, Q9, Q10, Q11]), "radius" : 3 * mm, "tangentPropagation" : true, "allowEdgeOverflow" : false});
        }
        {
            var Q0;
            Q0=makeQuery(id+"F1.opExtrude","CAP_FACE",FACE,{"disambiguationData":[OSD([sQuery(id+"F0.wireOp",EDGE,"E0.left"),sQuery(id+"F0.wireOp",EDGE,"E6"),sQuery(id+"F0.wireOp",EDGE,"E7"),sQuery(id+"F0.wireOp",EDGE,"E8"),sQuery(id+"F0.wireOp",EDGE,"E9"),sQuery(id+"F0.wireOp",EDGE,"E20"),sQuery(id+"F0.wireOp",EDGE,"E21"),sQuery(id+"F0.wireOp",EDGE,"E22"),sQuery(id+"F0.wireOp",EDGE,"E23"),sQuery(id+"F0.wireOp",EDGE,"E24"),sQuery(id+"F0.wireOp",EDGE,"E27"),sQuery(id+"F0.wireOp",EDGE,"E28"),sQuery(id+"F0.wireOp",EDGE,"E29"),sQuery(id+"F0.wireOp",EDGE,"E30"),sQuery(id+"F0.wireOp",EDGE,"E31"),sQuery(id+"F0.wireOp",EDGE,"E32"),sQuery(id+"F0.wireOp",EDGE,"E33"),sQuery(id+"F0.wireOp",EDGE,"E36"),sQuery(id+"F0.wireOp",EDGE,"E37"),sQuery(id+"F0.wireOp",EDGE,"E38"),sQuery(id+"F0.wireOp",EDGE,"E39"),sQuery(id+"F0.wireOp",EDGE,"E40"),sQuery(id+"F0.wireOp",EDGE,"E41"),sQuery(id+"F0.wireOp",EDGE,"E43"),sQuery(id+"F0.wireOp",EDGE,"E45.top"),sQuery(id+"F0.wireOp",EDGE,"E45.left"),sQuery(id+"F0.wireOp",EDGE,"E45.right"),sQuery(id+"F0.wireOp",EDGE,"E47.top"),sQuery(id+"F0.wireOp",EDGE,"E47.left"),sQuery(id+"F0.wireOp",EDGE,"E47.right"),sQuery(id+"F0.wireOp",EDGE,"E49.bottom"),sQuery(id+"F0.wireOp",EDGE,"E49.top"),sQuery(id+"F0.wireOp",EDGE,"E49.left"),sQuery(id+"F0.wireOp",EDGE,"E49.right"),sQuery(id+"F0.wireOp",EDGE,"E50.bottom"),sQuery(id+"F0.wireOp",EDGE,"E50.left"),sQuery(id+"F0.wireOp",EDGE,"E50.right"),sQuery(id+"F0.wireOp",EDGE,"E51"),sQuery(id+"F0.wireOp",EDGE,"E52"),sQuery(id+"F0.wireOp",EDGE,"E53"),sQuery(id+"F0.wireOp",EDGE,"E54"),sQuery(id+"F0.wireOp",EDGE,"E57"),sQuery(id+"F0.wireOp",EDGE,"E58"),sQuery(id+"F0.wireOp",EDGE,"E59.top"),sQuery(id+"F0.wireOp",EDGE,"E59.left"),sQuery(id+"F0.wireOp",EDGE,"E59.right"),sQuery(id+"F0.wireOp",EDGE,"E60.top"),sQuery(id+"F0.wireOp",EDGE,"E60.left"),sQuery(id+"F0.wireOp",EDGE,"E60.right")])],"isStart":false});
            var sketch = newSketch(context, id + "F7", { "sketchPlane" : qUnion([Q0])});
            skCircle(sketch, "E79", {"center": v(-30, 10) * mm, "radius": 3.3 * mm});
            skCircle(sketch, "E80", {"center": v(30, 10) * mm, "radius": 3.3 * mm});
            skCircle(sketch, "E81", {"center": v(30, -25) * mm, "radius": 3.3 * mm});
            skCircle(sketch, "E82", {"center": v(-30, -25) * mm, "radius": 3.3 * mm});
            skSolve(sketch);
        }
        {
            var Q0;
            Q0=makeQuery(id+"F7.imprint","IMPRINT",FACE,{"disambiguationData":[TD([[makeQuery(id+"F7.imprint","IMPRINT",EDGE,{"derivedFrom":sQuery(id+"F7.wireOp",EDGE,"E79")}),1.0]])]});
            var Q1;
            Q1=makeQuery(id+"F7.imprint","IMPRINT",FACE,{"disambiguationData":[TD([[makeQuery(id+"F7.imprint","IMPRINT",EDGE,{"derivedFrom":sQuery(id+"F7.wireOp",EDGE,"E80")}),1.0]])]});
            var Q2;
            Q2=makeQuery(id+"F7.imprint","IMPRINT",FACE,{"disambiguationData":[TD([[makeQuery(id+"F7.imprint","IMPRINT",EDGE,{"derivedFrom":sQuery(id+"F7.wireOp",EDGE,"E82")}),1.0]])]});
            var Q3;
            Q3=makeQuery(id+"F7.imprint","IMPRINT",FACE,{"disambiguationData":[TD([[makeQuery(id+"F7.imprint","IMPRINT",EDGE,{"derivedFrom":sQuery(id+"F7.wireOp",EDGE,"E81")}),1.0]])]});
            extrude(context, id + "F8", {"entities" : qUnion([Q0, Q1, Q2, Q3]), "operationType" : NewBodyOperationType.REMOVE, "oppositeDirection" : true, "depth" : 3 * mm, "offsetDistance" : 25 * mm});
        }
        {
            var Q0;
            Q0=makeQuery(id+"F0.imprint","IMPRINT",FACE,{"disambiguationData":[TD([[makeQuery(id+"F0.imprint","IMPRINT",EDGE,{"derivedFrom":sQuery(id+"F0.wireOp",EDGE,"E4")}),1.0]])]});
            var Q1;
            Q1=makeQuery(id+"F0.imprint","IMPRINT",FACE,{"disambiguationData":[TD([[makeQuery(id+"F0.imprint","IMPRINT",EDGE,{"derivedFrom":sQuery(id+"F0.wireOp",EDGE,"E5")}),1.0]])]});
            extrude(context, id + "F9", {"entities" : qUnion([Q0, Q1]), "operationType" : NewBodyOperationType.ADD, "flatOperationType" : FlatOperationType.REMOVE, "depth" : 18 * mm, "offsetDistance" : 25 * mm, "domain" : OperationDomain.MODEL});
        }
        {
            var Q0;
            Q0=makeQuery(id+"F0.imprint","IMPRINT",FACE,{"disambiguationData":[TD([[makeQuery(id+"F0.imprint","IMPRINT",EDGE,{"derivedFrom":sQuery(id+"F0.wireOp",EDGE,"E45.top")}),1.0]])]});
            var Q1;
            Q1=makeQuery(id+"F0.imprint","IMPRINT",FACE,{"disambiguationData":[TD([[makeQuery(id+"F0.imprint","IMPRINT",EDGE,{"derivedFrom":sQuery(id+"F0.wireOp",EDGE,"E50.bottom")}),1.0]])]});
            var Q2;
            {var subQ3=sQuery(id+"F0.wireOp",EDGE,"E49.bottom");Q2=makeQuery(id+"F0.imprint","IMPRINT",FACE,{"disambiguationData":[TD([[makeQuery(id+"F0.imprint","IMPRINT",EDGE,{"derivedFrom":subQ3}),-1.0]])]});}
            var Q3;
            Q3=makeQuery(id+"F0.imprint","IMPRINT",FACE,{"disambiguationData":[TD([[makeQuery(id+"F0.imprint","IMPRINT",EDGE,{"derivedFrom":sQuery(id+"F0.wireOp",EDGE,"E47.top")}),-1.0]])]});
            extrude(context, id + "F10", {"entities" : qUnion([Q0, Q1, Q2, Q3]), "operationType" : NewBodyOperationType.ADD, "depth" : 15.5 * mm, "offsetDistance" : 25 * mm});
        }
    });
